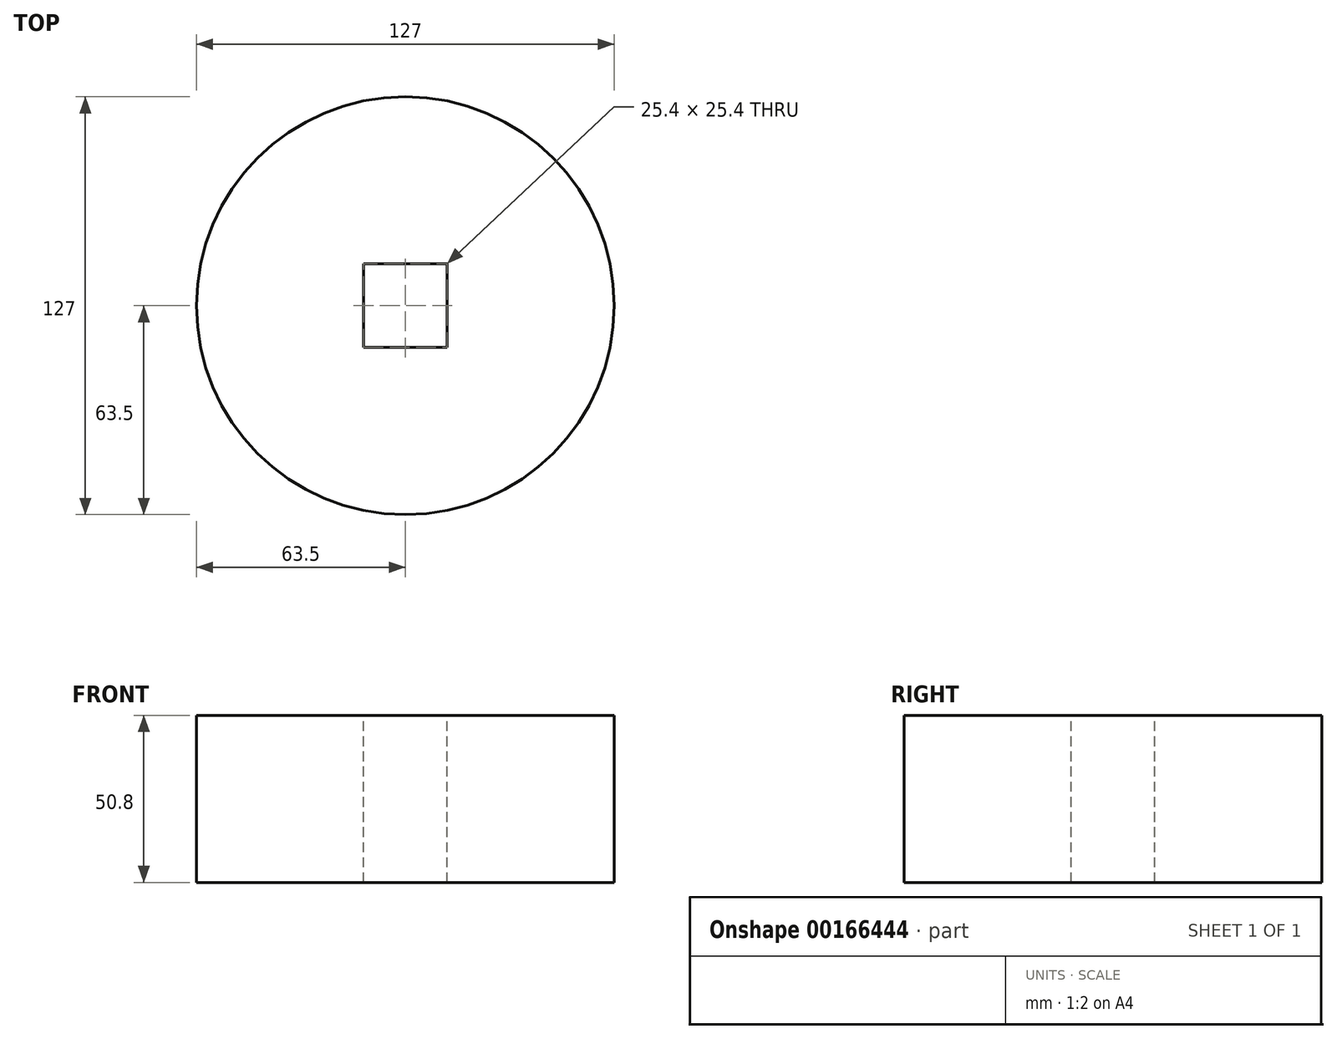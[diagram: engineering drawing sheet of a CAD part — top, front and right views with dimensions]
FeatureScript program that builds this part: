
annotation { "Feature Type Name" : "Feature", "Feature Type Description" : "" }
export const myFeature = defineFeature(function(context is Context, id is Id, definition is map)
    precondition{}
    {
        {
            var Q0;
            Q0=qCreatedBy(makeId("Top.planeOp"),FACE);
            var sketch = newSketch(context, id + "F0", { "sketchPlane" : qUnion([Q0])});
            skCircle(sketch, "E0", {"center": v(0, 0) * mm, "radius": 63.5 * mm});
            skSolve(sketch);
        }
        {
            var Q0;
            Q0 = qSketchRegion(id + "F0", true);
            extrude(context, id + "F1", {"entities" : qUnion([Q0]), "depth" : 50.8 * mm});
        }
        {
            var Q0;
            Q0=makeQuery(id+"F1.opExtrude","CAP_FACE",FACE,{"disambiguationData":[OSD([sQuery(id+"F0.wireOp",EDGE,"E0")])],"isStart":false});
            var sketch = newSketch(context, id + "F2", { "sketchPlane" : qUnion([Q0])});
            skLineSegment(sketch, "E1.bottom", {"start": v(12.7, 12.7) * mm, "end": v(-12.7, 12.7) * mm});
            skLineSegment(sketch, "E1.top", {"start": v(12.7, -12.7) * mm, "end": v(-12.7, -12.7) * mm});
            skLineSegment(sketch, "E1.left", {"start": v(12.7, 12.7) * mm, "end": v(12.7, -12.7) * mm});
            skLineSegment(sketch, "E1.right", {"start": v(-12.7, 12.7) * mm, "end": v(-12.7, -12.7) * mm});
            skPoint(sketch, "E1.middle", {"position": v(0, 0) * mm});
            skSolve(sketch);
        }
        {
            var Q0;
            Q0 = qSketchRegion(id + "F2", true);
            extrude(context, id + "F3", {"entities" : qUnion([Q0]), "operationType" : NewBodyOperationType.REMOVE, "endBound" : BoundingType.THROUGH_ALL, "oppositeDirection" : true, "depth" : 25.4 * mm});
        }
    });
